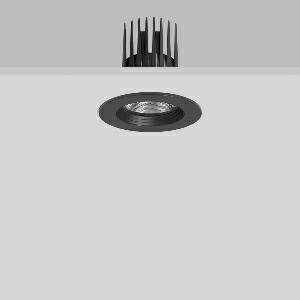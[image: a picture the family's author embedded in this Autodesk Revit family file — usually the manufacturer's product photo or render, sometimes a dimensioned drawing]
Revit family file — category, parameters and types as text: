
# Revit family: heledon_mini_e_901741_003_3_76_cbac
name_source: partatom
category: Lighting Fixtures
units: mm (PartAtom-declared; Revit-internal decimal feet)

## family parameters
Cut with Voids When Loaded = No
Host = Face
Light Source = No
Part Type = Normal
Room Calculation Point = No
Round Connector Dimension = Use Diameter
Shared = No

## types (1)
- HELEDON mini E (1 x LED Modul 935, 2500 lm, 3500)
    Apparent Load = 20 VA
    Approval mark = CE
    CIE Flux Codes = 99 100 100 100 100
    Color Rendering = 92
    Color Temperature = 3500
    Default Elevation = 1800 mm
    Description = Series: HELEDON mini
Round recessed downlight. Housing: die-cast aluminium, powder-coated. Black plastic ring and recessed LED to prevent glare from the side. Optical assembly with reflector made of MIRO-Silver with 98% total light reflection for outstanding efficiency - can be changed without tools. Best colour rendering index Ra>90. Suitable for Recessed ceiling mounting. Installation without tools thanks to spring fastening system. Including separate LED converter with connecting cable 600 mm.High quality converter without flickering and stroboscopic effect. Through-wiring box (5 pole) available as accessory. The following accessories can be mounted without use of tools: interchangeable lenses, decorative glasses, honeycomb louvre, clear and frosted diffusers, white interchangeable plastic ring. 
Colour: deep black, matt (RAL 9005)
Diameter: 124 mm
Height: 3 mm
Cut-out diameter: 114 mm
Recess height: 170 mm
Luminaire: recess height: 120 mm
Lamp: LED
Socket: without socket
Colour temperature: 3500K
Colour rendering index (CRI): 92
System power: 20 W
Rated luminous flux: 2500 lm
Luminous efficiency: 125 lm/W
Control gear: Converter, dimmable, DALI
Protection class: II
Type of protection: IP 20
    Height = 0 mm  [stored 0 ft]
    Lamp = 1 x LED Modul 935
    Lamp Light Flux = 2500 lm
    Lamp count = 1
    Length = 124 mm  [stored 0.406824 ft]
    Lifetime = 50000 h
    Luminous efficacy = 125 lm/W
    Manufacturer = RZB
    ModVariant = No
    Model = 901741.003.3.76
    Mounting Place = Ceiling
    Mounting Type = Recessed
    Number of Poles = 1
    OnlyDefault = Yes
    Power Factor = 1
    Product Name = HELEDON mini E
    Product group = Recessed downlights
    ProductGroupID = 402
    Protection Class = Protection class II
    Protection Degree = IP 20
    RLX_Detail_Level = 1
    RLX_Emergency_Light_Flux = 0 lm
    RLX_Emergency_Type = 0
    RLX_Emergency_Type_DB = No
    RlxData = <blob elided: 126141 chars, md5=1f58b6c6>
    Socket = socket
    Standby Power = 0 W
    System Light Flux = 2500 lm
    System Power = 20 W
    Type Comments = Product without accessories
    Type Image = 901657.003.jpg
    URL = http://relux.com
    VarID = ---
    Voltage = 230 V
    Voltage Range = 220-240 V
    Weight = 0.00 kg
    Width = 0 mm  [stored 0 ft]

note: [stored X ft] marks values corroborated as IEEE doubles in the binary element streams (Revit-internal decimal feet)

## geometry (parser evidence)
native form markers: Blend x4, Sweep x11
no freeform markers — native parametric forms only
